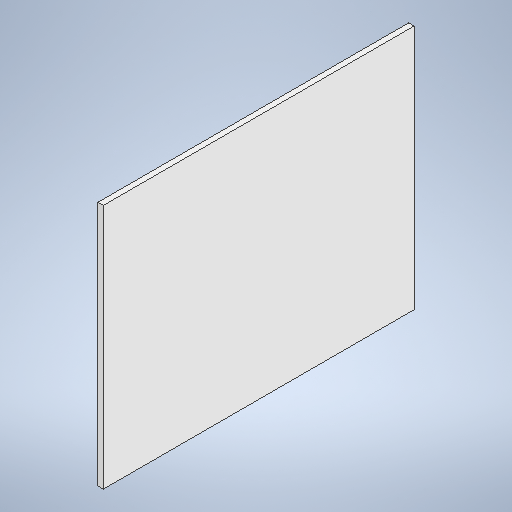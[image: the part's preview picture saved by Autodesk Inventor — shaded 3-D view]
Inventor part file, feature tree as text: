
AUTODESK INVENTOR PART (.ipt)
format: ipt  version: 2025 (Build 290162000, 162)  size: 229,888 bytes
history: native  units: in
note: dims shown in document units (in); Inventor stores cm internally (conversion verified against a paired STEP export)
features: extrude x1, sketch x1
ambient origin geometry x8: Origin, YZ Plane, XZ Plane, XY Plane, X Axis, Y Axis, Z Axis, Center Point
bodies: Solid1 (feature_tree)
feature tree (2):
  extrude  "Extrusion1"  Depth=34.0in
  sketch  "Sketch1"  dims[d1=43.0in d2=34.0in d3=0.75in d4=0.0in]
